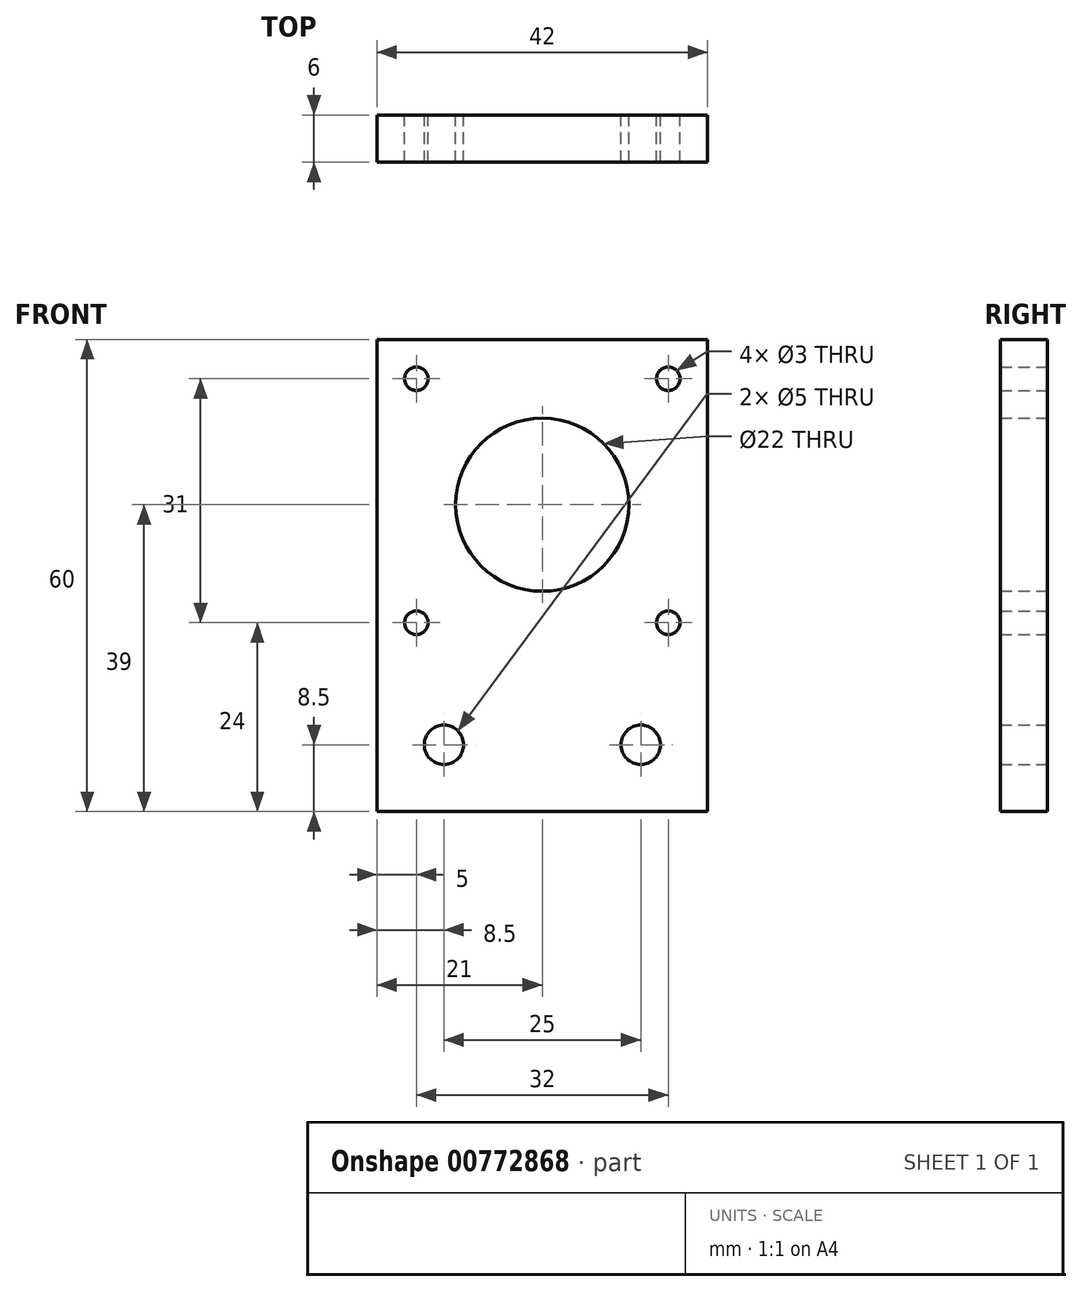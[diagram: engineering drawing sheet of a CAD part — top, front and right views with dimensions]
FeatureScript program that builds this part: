
annotation { "Feature Type Name" : "Feature", "Feature Type Description" : "" }
export const myFeature = defineFeature(function(context is Context, id is Id, definition is map)
    precondition{}
    {
        {
            var Q0;
            Q0=qCreatedBy(makeId("Front.planeOp"),FACE);
            var sketch = newSketch(context, id + "F0", { "sketchPlane" : qUnion([Q0])});
            skLineSegment(sketch, "E0.bottom", {"start": v(-21, 39) * mm, "end": v(21, 39) * mm});
            skLineSegment(sketch, "E0.top", {"start": v(-21, -21) * mm, "end": v(21, -21) * mm});
            skLineSegment(sketch, "E0.left", {"start": v(-21, 39) * mm, "end": v(-21, -21) * mm});
            skLineSegment(sketch, "E0.right", {"start": v(21, 39) * mm, "end": v(21, -21) * mm});
            skCircle(sketch, "E1", {"center": v(16, 34) * mm, "radius": 1.5 * mm});
            skCircle(sketch, "E2", {"center": v(16, 3) * mm, "radius": 1.5 * mm});
            skCircle(sketch, "E3.MirrorC", {"center": v(-16, 34) * mm, "radius": 1.5 * mm});
            skCircle(sketch, "E4.MirrorC", {"center": v(-16, 3) * mm, "radius": 1.5 * mm});
            skCircle(sketch, "E5", {"center": v(0, 18) * mm, "radius": 11 * mm});
            skCircle(sketch, "E6", {"center": v(12.5, -12.5) * mm, "radius": 2.5 * mm});
            skCircle(sketch, "E7.MirrorC", {"center": v(-12.5, -12.5) * mm, "radius": 2.5 * mm});
            skSolve(sketch);
        }
        {
            var Q0;
            Q0 = qSketchRegion(id + "F0", true);
            extrude(context, id + "F1", {"entities" : qUnion([Q0]), "depth" : 6 * mm, "offsetDistance" : 25 * mm});
        }
    });
